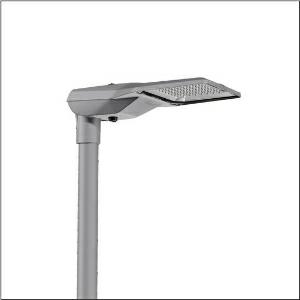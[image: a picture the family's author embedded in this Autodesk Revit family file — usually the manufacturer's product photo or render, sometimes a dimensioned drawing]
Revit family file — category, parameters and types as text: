
# Revit family: streetlight_sl_21_iq_midi___p0_8a_5xe3u31y08nb_1433
name_source: partatom
category: Lighting Fixtures
units: mm (PartAtom-declared; Revit-internal decimal feet)

## family parameters
Cut with Voids When Loaded = No
Host = Face
Light Source = No
Part Type = Normal
Room Calculation Point = No
Round Connector Dimension = Use Diameter
Shared = No

## types (1)
- --- (1 x LED, 21740 lm, 136.6 W, 3000K)
    Apparent Load = 137 VA
    CIE Flux Codes = 36 69 97 100 100
    Color Rendering = 70
    Color Temperature = 3000K
    Default Elevation = 1800 mm
    Description = Streetlight SL 21 iQ midi, mast luminaire, primary light control with lens, of PMMA, primary optical cover: cover, of toughened safety glass, transparent, light distribution: P0.8a, light emission: direct distribution, primary light characteristic: asymmetric, installation type: post-top, side-entry, LED, High Power LED, rated luminous flux: 21.740lm, luminous efficacy: 159lm/W, light colour: 730, colour temperature: 3000K, control gear: iQ-Street Remote, D4i with power reduction, control: pre-setting: logarithmic dimming characteristic, Street-Remote, Auto-Match, Temp-Guard, Lumen-Switch, Night-Set, Smart-Wire, Light-Fading, Desk-Remote (wireless, voltage-free reading and setting of iQ features in the workshop via application-optimized NFC function/RFID function), optimised constant luminous flux control (CLO 2.0), mains connection: 230..240V, AC, 50/60Hz, start of lifetime: 137W, end of service life: 144W, reduction: 61W, luminaire housing, of diecast aluminium, powder-coated, SITECO metallic grey (DB 702S), corrosivity category C5 high according to DIN EN ISO 12944, please order mast flange separately, inclination adjustable: 0°, 5°, 10°, 15°, sealing non-destructively replaceable, multi-level sealing system, length: 644mm, width: 335mm, height: 110mm, mast flange for spigot size: 42mm (side-entry): 5XC10008XM4, 60/48mm (side-entry/post-top): 5XC10108XM2, 76/60mm (side-entry/post-top): 5XC10108XM1, mounting height: 4..8m, Smart Interface below and above, protection rating (complete): IP66, insulation class (complete): insulation class II (safety insulation), certification: CE, ENEC, ENEC+, VDE, impact resistance: IK10, permissible operating ambient temperature for outdoor applications: -40..+50°C, standard-compliant lighting for roads and squares, packaging unit: 1 piece

Light Distribution: P0.8a
    Height = 111 mm
    Lamp = 1 x LED
    Lamp Light Flux = 21740 lm
    Lamp Power = 136.6 W
    Lamp count = 1
    Length = 644 mm
    Luminous efficacy = 159 lm/W
    Manufacturer = Siteco
    ModVariant = No
    Model = 5XE3U31Y08NB
    Number of Poles = 1
    OnlyDefault = Yes
    Power Factor = 1
    Product Name = Streetlight SL 21 iQ midi | P0.8a
    Product group = mast luminaire | pylon top
    ProductGroupID = 6100
    Protection Class = Protection class II
    Protection Degree = IP 66
    RLX_Detail_Level = 1
    RLX_Emergency_Light_Flux = 0 lm
    RLX_Emergency_Type = 0
    RLX_Emergency_Type_DB = No
    RlxData = <blob elided: 91041 chars, md5=783798e3>
    Socket = socket
    Standby Power = 0 W
    System Light Flux = 21740 lm
    System Power = 137 W
    Type Comments = factory setting: luminous flux: 100 % | dim-lin: 254 | 733 mA
    Type Image = l_1004304.jpg
    URL = http://relux.com
    VarID = @adj_079725
    Voltage = 0 V
    Weight = 0.00 kg
    Width = 336 mm

## geometry (parser evidence)
native form markers: Blend x4, Sweep x12
no freeform markers — native parametric forms only
